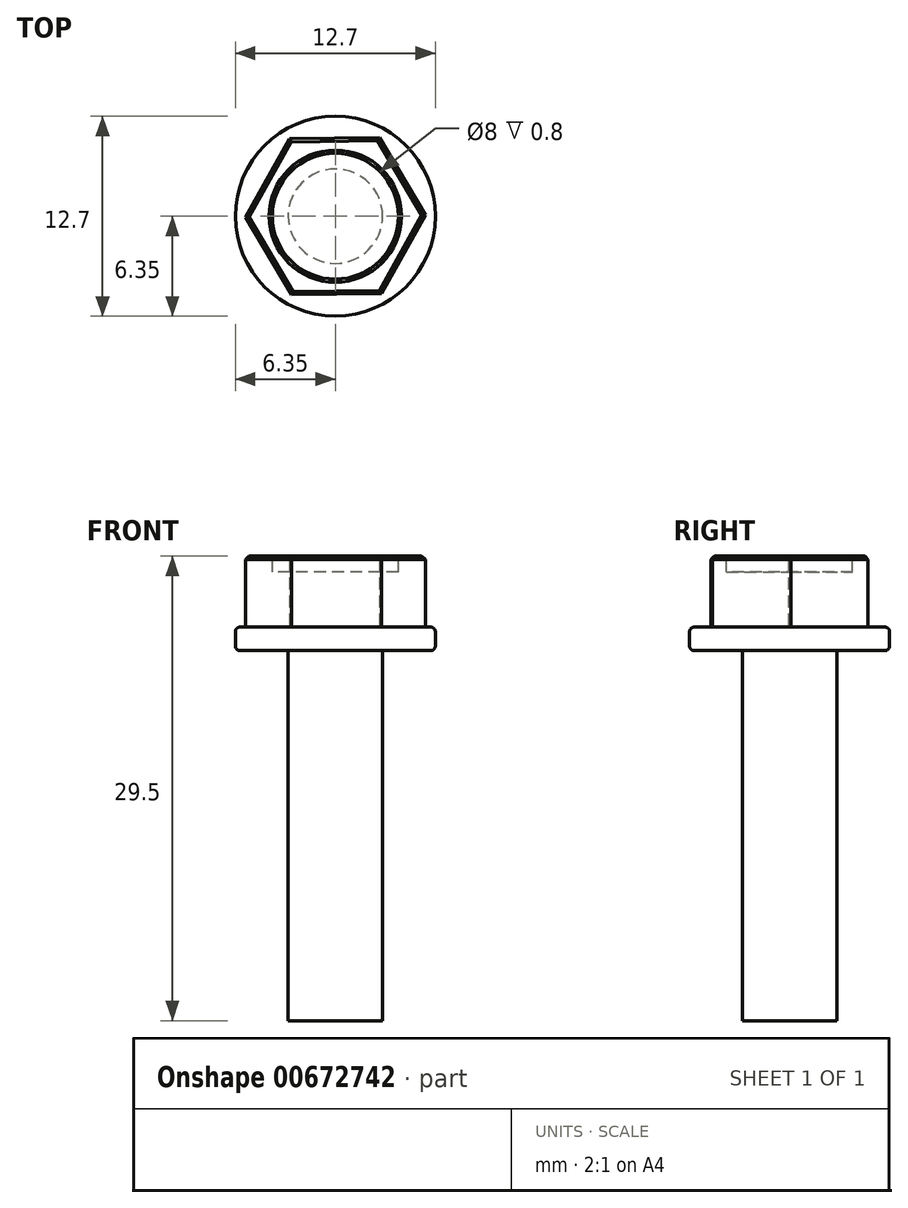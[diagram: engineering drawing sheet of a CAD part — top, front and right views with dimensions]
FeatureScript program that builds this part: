
annotation { "Feature Type Name" : "Feature", "Feature Type Description" : "" }
export const myFeature = defineFeature(function(context is Context, id is Id, definition is map)
    precondition{}
    {
        {
            var Q0;
            Q0=qCreatedBy(makeId("Top.planeOp"),FACE);
            var sketch = newSketch(context, id + "F0", { "sketchPlane" : qUnion([Q0])});
            skCircle(sketch, "E0.cCircle", {"center": v(0, 0) * mm, "radius": 4.95 * mm, "construction": true});
            skLineSegment(sketch, "E0.0", {"start": v(5.72, 0.07) * mm, "end": v(2.92, -4.91) * mm});
            skLineSegment(sketch, "E0.1", {"start": v(2.92, -4.91) * mm, "end": v(-2.8, -4.99) * mm});
            skLineSegment(sketch, "E0.2", {"start": v(-2.8, -4.99) * mm, "end": v(-5.72, -0.07) * mm});
            skLineSegment(sketch, "E0.3", {"start": v(-5.72, -0.07) * mm, "end": v(-2.92, 4.91) * mm});
            skLineSegment(sketch, "E0.4", {"start": v(-2.92, 4.91) * mm, "end": v(2.8, 4.99) * mm});
            skLineSegment(sketch, "E0.5", {"start": v(2.8, 4.99) * mm, "end": v(5.72, 0.07) * mm});
            skPoint(sketch, "E0.0.midPoint", {"position": v(4.32, -2.42) * mm});
            skCircle(sketch, "E1", {"center": v(0, 0) * mm, "radius": 6.35 * mm});
            skCircle(sketch, "E2", {"center": v(0, 0) * mm, "radius": 3 * mm});
            skSolve(sketch);
        }
        {
            var Q0;
            Q0=makeQuery(id+"F0.imprint","IMPRINT",FACE,{"disambiguationData":[TD([[makeQuery(id+"F0.imprint","IMPRINT",EDGE,{"derivedFrom":sQuery(id+"F0.wireOp",EDGE,"E0.0")}),-1.0]])]});
            var Q1;
            Q1=makeQuery(id+"F0.imprint","IMPRINT",FACE,{"disambiguationData":[TD([[makeQuery(id+"F0.imprint","IMPRINT",EDGE,{"derivedFrom":sQuery(id+"F0.wireOp",EDGE,"E2")}),1.0]])]});
            extrude(context, id + "F1", {"entities" : qUnion([Q0, Q1]), "depth" : 4.5 * mm, "offsetDistance" : 25 * mm});
        }
        {
            var Q0;
            Q0=makeQuery(id+"F0.imprint","IMPRINT",FACE,{"disambiguationData":[TD([[makeQuery(id+"F0.imprint","IMPRINT",EDGE,{"derivedFrom":sQuery(id+"F0.wireOp",EDGE,"E0.0")}),1.0]])]});
            var Q1;
            Q1=makeQuery(id+"F0.imprint","IMPRINT",FACE,{"disambiguationData":[TD([[makeQuery(id+"F0.imprint","IMPRINT",EDGE,{"derivedFrom":sQuery(id+"F0.wireOp",EDGE,"E2")}),1.0]])]});
            var Q2;
            Q2=makeQuery(id+"F0.imprint","IMPRINT",FACE,{"disambiguationData":[TD([[makeQuery(id+"F0.imprint","IMPRINT",EDGE,{"derivedFrom":sQuery(id+"F0.wireOp",EDGE,"E0.0")}),-1.0]])]});
            extrude(context, id + "F2", {"entities" : qUnion([Q0, Q1, Q2]), "operationType" : NewBodyOperationType.ADD, "oppositeDirection" : true, "depth" : 1.5 * mm, "offsetDistance" : 25 * mm});
        }
        {
            var Q0;
            Q0=makeQuery(id+"F0.imprint","IMPRINT",FACE,{"disambiguationData":[TD([[makeQuery(id+"F0.imprint","IMPRINT",EDGE,{"derivedFrom":sQuery(id+"F0.wireOp",EDGE,"E2")}),1.0]])]});
            extrude(context, id + "F3", {"entities" : qUnion([Q0]), "operationType" : NewBodyOperationType.ADD, "oppositeDirection" : true, "depth" : 25 * mm, "offsetDistance" : 25 * mm});
        }
        {
            var Q0;
            Q0=makeQuery(id+"F2.opExtrude","SWEPT_FACE",FACE,{"disambiguationData":[OSD([sQuery(id+"F0.wireOp",EDGE,"E1")])]});
            fillet(context, id + "F4", {"entities" : qUnion([Q0]), "tangentPropagation" : true, "radius" : 0.3 * mm, "defaultsChanged" : true, "vertexSettings" : [], "allowEdgeOverflow" : false});
        }
        {
            var Q0;
            Q0=makeQuery(id+"F1.opExtrude","CAP_FACE",FACE,{"disambiguationData":[OSD([sQuery(id+"F0.wireOp",EDGE,"E0.0"),sQuery(id+"F0.wireOp",EDGE,"E0.1"),sQuery(id+"F0.wireOp",EDGE,"E0.2"),sQuery(id+"F0.wireOp",EDGE,"E0.3"),sQuery(id+"F0.wireOp",EDGE,"E0.4"),sQuery(id+"F0.wireOp",EDGE,"E0.5")])],"isStart":false});
            var sketch = newSketch(context, id + "F5", { "sketchPlane" : qUnion([Q0])});
            skCircle(sketch, "E3", {"center": v(0, 0) * mm, "radius": 4 * mm});
            skSolve(sketch);
        }
        {
            var Q0;
            Q0 = qSketchRegion(id + "F5", true);
            extrude(context, id + "F6", {"entities" : qUnion([Q0]), "operationType" : NewBodyOperationType.REMOVE, "oppositeDirection" : true, "depth" : 1 * mm, "offsetDistance" : 25 * mm});
        }
        {
            var Q0;
            Q0=makeQuery(id+"F1.opExtrude","CAP_FACE",FACE,{"disambiguationData":[OSD([sQuery(id+"F0.wireOp",EDGE,"E0.0"),sQuery(id+"F0.wireOp",EDGE,"E0.1"),sQuery(id+"F0.wireOp",EDGE,"E0.2"),sQuery(id+"F0.wireOp",EDGE,"E0.3"),sQuery(id+"F0.wireOp",EDGE,"E0.4"),sQuery(id+"F0.wireOp",EDGE,"E0.5")])],"isStart":false});
            chamfer(context, id + "F7", {"entities" : qUnion([Q0]), "width" : 0.2 * mm, "tangentPropagation" : true});
        }
    });
